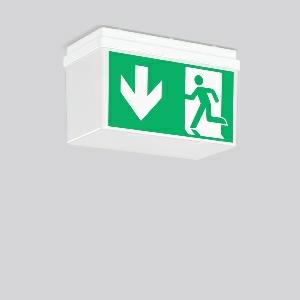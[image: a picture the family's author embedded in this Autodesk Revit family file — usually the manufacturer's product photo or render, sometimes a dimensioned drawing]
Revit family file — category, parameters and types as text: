
# Revit family: gsun_3_672520_002_07_0847
name_source: partatom
category: Lighting Fixtures
units: mm (PartAtom-declared; Revit-internal decimal feet)

## family parameters
Cut with Voids When Loaded = No
Host = Face
Light Source = No
Part Type = Normal
Room Calculation Point = No
Round Connector Dimension = Use Diameter
Shared = No

## types (1)
- GSUN 3 (1 x LED Modul 840, 200 lm, 4000)
    Apparent Load = 4 VA
    Approval mark = CE
    CIE Flux Codes = 31 59 82 69 100
    Color Rendering = 80
    Color Temperature = 4000
    Default Elevation = 1800 mm
    Description = Series: GSUN 3
Luminaire for escape route identification. Base: plastic Diffuser: plastic, opal 4 plastic foils with escape route motifs included (ISO 7010). Suitable for Ceiling mounting, Wall (surface). Pendant luminaire also possible with accessories. Electronic ballast included. Self-contained system with automatic self-test and feedback via DALI bus, only to RZB DALI monitoring system. 
Colour: white
Length: 241 mm
Width: 126 mm
Height: 147 mm
Weight: 440 g
Operating mode: maintained power mode
Viewing Distance: 21 m
Duration time: 3 h
Lamp: LED
Socket: without socket
Colour temperature: 4000K
Colour rendering index (CRI): 80
System power: 4 W
Control gear: EB
Protection class: II
Type of protection: IP 54
    Height = 147 mm
    Lamp = 1 x LED Modul 840
    Lamp Light Flux = 200 lm
    Lamp count = 1
    Length = 241 mm
    Lifetime = 50000 h
    Luminous efficacy = 49 lm/W
    Manufacturer = RZB
    ModVariant = No
    Model = 672520.002.07
    Mounting Place = Ceiling, Wall
    Mounting Type = Surface mounted
    Number of Poles = 1
    OnlyDefault = Yes
    Power Factor = 1
    Product Name = GSUN 3
    Product group = Surface mounted ceiling and wall luminaires
    ProductGroupID = 305
    Protection Class = Protection class II
    Protection Degree = IP 54
    RLX_Detail_Level = 1
    RLX_Emergency_Light_Flux = 100 lm
    RLX_Emergency_Type = 3
    RLX_Emergency_Type_DB = Yes
    RlxData = <blob elided: 40585 chars, md5=9e2dd581>
    Socket = socket
    Standby Power = 0 W
    System Light Flux = 200 lm
    System Power = 4 W
    Type Comments = Product without accessories
    Type Image = 672520.002.jpg
    URL = http://relux.com
    VarID = ---
    Voltage = 230 V
    Voltage Range = 220-240 V
    Weight = 0.00 kg
    Width = 126 mm

## geometry (parser evidence)
native form markers: Blend x4, Sweep x13
no freeform markers — native parametric forms only
